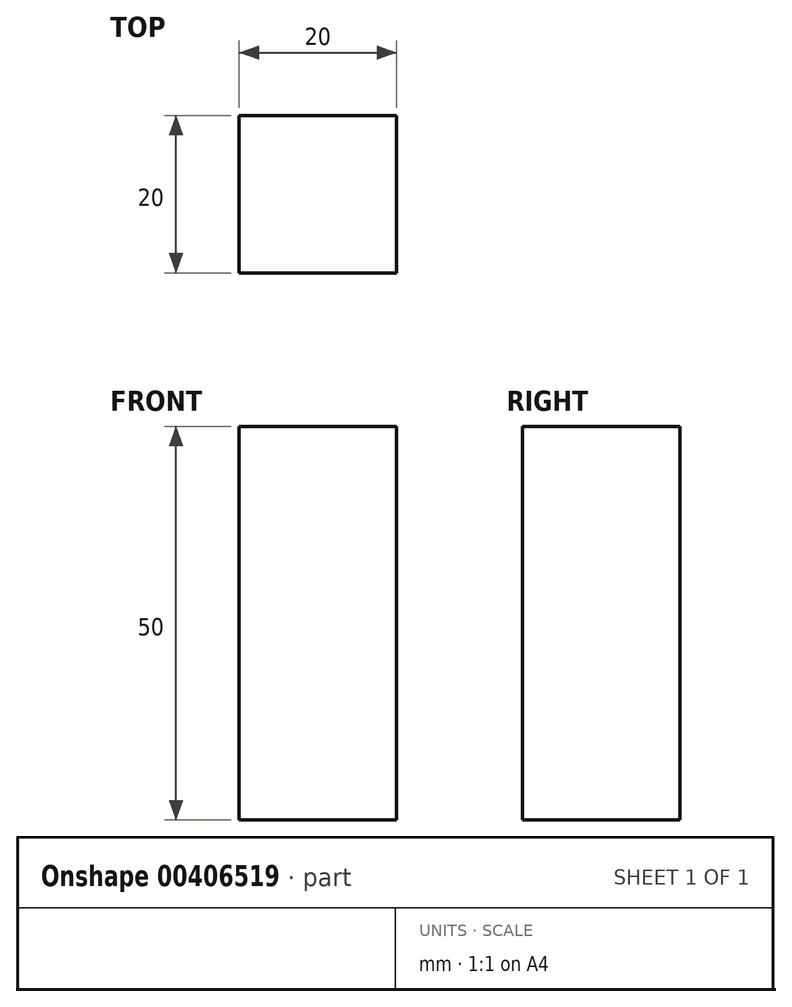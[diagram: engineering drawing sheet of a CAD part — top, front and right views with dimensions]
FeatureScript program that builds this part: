
annotation { "Feature Type Name" : "Feature", "Feature Type Description" : "" }
export const myFeature = defineFeature(function(context is Context, id is Id, definition is map)
    precondition{}
    {
        {
            var Q0;
            Q0=qCreatedBy(makeId("Top.planeOp"),FACE);
            var sketch = newSketch(context, id + "F0", { "sketchPlane" : qUnion([Q0])});
            skLineSegment(sketch, "E0.bottom", {"start": v(10, 10) * mm, "end": v(-10, 10) * mm});
            skLineSegment(sketch, "E0.top", {"start": v(10, -10) * mm, "end": v(-10, -10) * mm});
            skLineSegment(sketch, "E0.left", {"start": v(10, 10) * mm, "end": v(10, -10) * mm});
            skLineSegment(sketch, "E0.right", {"start": v(-10, 10) * mm, "end": v(-10, -10) * mm});
            skPoint(sketch, "E0.middle", {"position": v(0, 0) * mm});
            skSolve(sketch);
        }
        {
            var Q0;
            Q0 = qSketchRegion(id + "F0", true);
            extrude(context, id + "F1", {"entities" : qUnion([Q0]), "depth" : 50 * mm});
        }
    });
